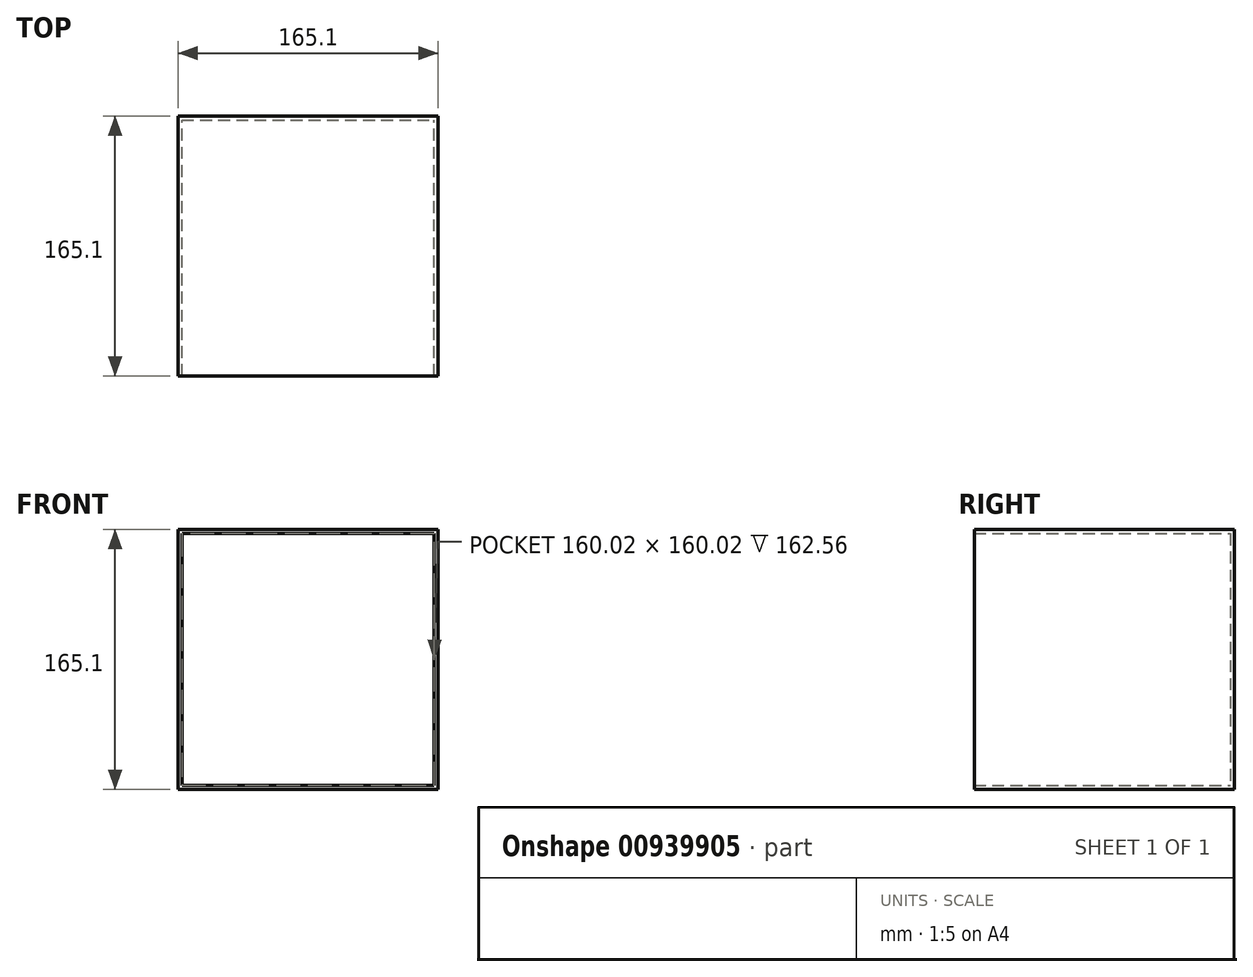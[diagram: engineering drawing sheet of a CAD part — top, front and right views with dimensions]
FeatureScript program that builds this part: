
annotation { "Feature Type Name" : "Feature", "Feature Type Description" : "" }
export const myFeature = defineFeature(function(context is Context, id is Id, definition is map)
    precondition{}
    {
        {
            assignVariable(context, id + "F0", {"name" : "size", "anyValue" : 165.1 * mm});
        }
        {
            var Q0;
            Q0=qCreatedBy(makeId("Front.planeOp"),FACE);
            var sketch = newSketch(context, id + "F1", { "sketchPlane" : qUnion([Q0])});
            skLineSegment(sketch, "E0.bottom", {"start": v(-82.55, 82.55) * mm, "end": v(82.55, 82.55) * mm});
            skLineSegment(sketch, "E0.top", {"start": v(-82.55, -82.55) * mm, "end": v(82.55, -82.55) * mm});
            skLineSegment(sketch, "E0.left", {"start": v(-82.55, 82.55) * mm, "end": v(-82.55, -82.55) * mm});
            skLineSegment(sketch, "E0.right", {"start": v(82.55, 82.55) * mm, "end": v(82.55, -82.55) * mm});
            skPoint(sketch, "E0.middle", {"position": v(0, 0) * mm});
            skSolve(sketch);
        }
        {
            var Q0;
            Q0=makeQuery(id+"F1.imprint","IMPRINT",FACE,{"disambiguationData":[TD([[makeQuery(id+"F1.imprint","IMPRINT",EDGE,{"derivedFrom":sQuery(id+"F1.wireOp",EDGE,"E0.bottom")}),-1.0]])]});
            extrude(context, id + "F2", {"entities" : qUnion([Q0]), "depth" : getVariable(context, 'size'), "offsetDistance" : 25.4 * mm});
        }
        {
            var Q0;
            Q0=makeQuery(id+"F2.opExtrude","CAP_FACE",FACE,{"disambiguationData":[OSD([sQuery(id+"F1.wireOp",EDGE,"E0.bottom"),sQuery(id+"F1.wireOp",EDGE,"E0.top"),sQuery(id+"F1.wireOp",EDGE,"E0.left"),sQuery(id+"F1.wireOp",EDGE,"E0.right")])],"isStart":false});
            shell(context, id + "F3", {"entities" : qUnion([Q0]), "thickness" : 2.54 * mm});
        }
    });
